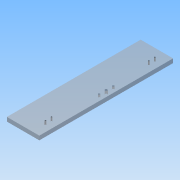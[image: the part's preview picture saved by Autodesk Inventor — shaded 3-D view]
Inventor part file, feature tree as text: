
AUTODESK INVENTOR PART (.ipt)
format: ipt  version: 2016 (Build 200138000, 138)  size: 109,056 bytes
history: native  units: mm
features: hole x4, sketch x4, extrude x1, pattern_linear x1
ambient origin geometry x8: Origin, YZ Plane, XZ Plane, XY Plane, X Axis, Y Axis, Z Axis, Center Point
bodies: Volumenkörper1 (feature_tree)
feature tree (10):
  extrude  "Extrusion1"  Depth=360.0mm
  hole  "Bohrung2"  [1 undecoded]
  hole  "Bohrung3"  [1 undecoded]
  hole  "Bohrung4"  [1 undecoded]
  pattern_linear  "Rechteckige Anordnung2"  Count1=3  [1 undecoded]
  hole  "Bohrung5"  [1 undecoded]
  sketch  "Skizze1"  dims[d0=80.0mm d1=360.0mm]
  sketch  "Skizze3"  dims[d2=10.0mm d3=0.0mm d16=15.0mm]
  sketch  "Skizze4"  dims[d17=70.0mm]
  sketch  "Skizze5"  dims[d18=6.0mm d19=6.0mm d20=4.0mm d21=2.0mm d22=90.0deg d23=8.0mm d24=20.594885mm d25=35.0mm d27=4.5mm d28=6.0mm d29=10.0mm d30=2.0mm d31=90.0deg d32=8.0mm d33=20.594885mm d34=15.0mm d35=30.0mm d36=55.0mm d37=3.242mm d38=6.0mm d39=4.0mm d40=2.0mm d41=90.0deg d42=8.0mm d43=20.594885mm d44=20.0mm d46=200.0mm d47=5.0mm d48=3.242mm d49=8.0mm d50=4.0mm d51=2.0mm d52=90.0deg d53=10.0mm d54=20.594885mm]
note: 5 required parameter values undecoded (feature->parameter linkage not recoverable at this tier; creation-order binding heuristic only, values carry confidence <= 0.55)
